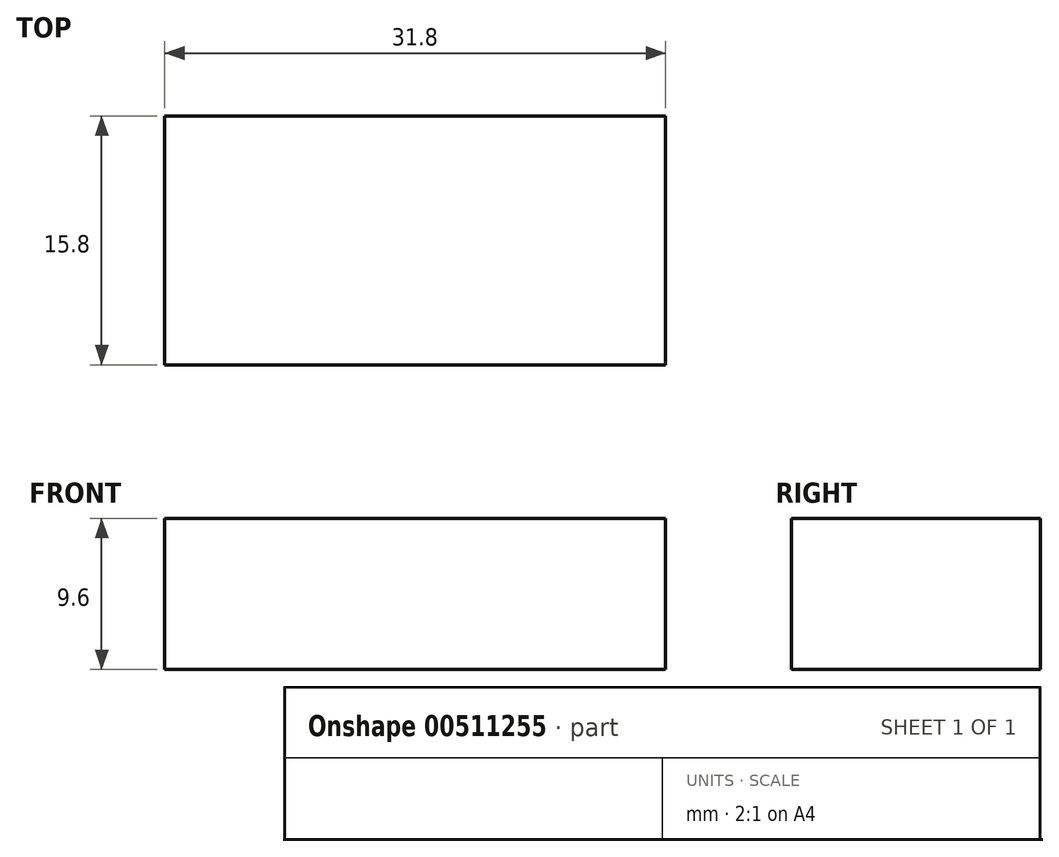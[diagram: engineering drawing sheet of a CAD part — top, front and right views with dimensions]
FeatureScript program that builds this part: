
annotation { "Feature Type Name" : "Feature", "Feature Type Description" : "" }
export const myFeature = defineFeature(function(context is Context, id is Id, definition is map)
    precondition{}
    {
        {
            var Q0;
            Q0=qCreatedBy(makeId("Front.planeOp"),FACE);
            var sketch = newSketch(context, id + "F0", { "sketchPlane" : qUnion([Q0])});
            skLineSegment(sketch, "E0.bottom", {"start": v(-15.9, 4.8) * mm, "end": v(15.9, 4.8) * mm});
            skLineSegment(sketch, "E0.top", {"start": v(-15.9, -4.8) * mm, "end": v(15.9, -4.8) * mm});
            skLineSegment(sketch, "E0.left", {"start": v(-15.9, 4.8) * mm, "end": v(-15.9, -4.8) * mm});
            skLineSegment(sketch, "E0.right", {"start": v(15.9, 4.8) * mm, "end": v(15.9, -4.8) * mm});
            skPoint(sketch, "E0.middle", {"position": v(0, 0) * mm});
            skSolve(sketch);
        }
        {
            var Q0;
            Q0 = qSketchRegion(id + "F0", true);
            extrude(context, id + "F1", {"entities" : qUnion([Q0]), "endBound" : BoundingType.SYMMETRIC, "depth" : 15.8 * mm});
        }
    });
